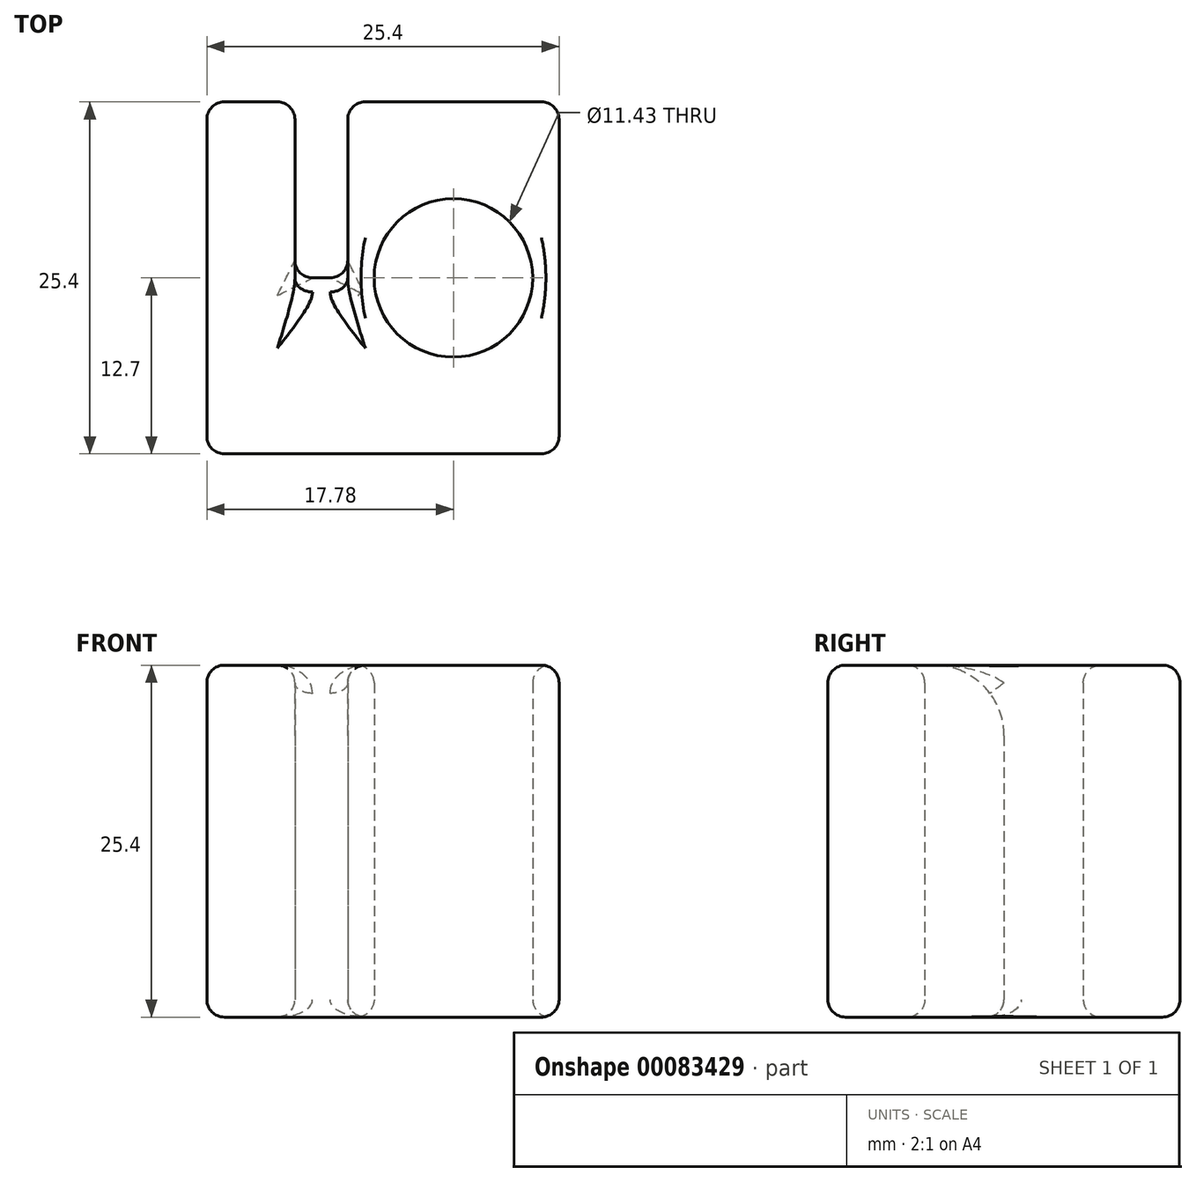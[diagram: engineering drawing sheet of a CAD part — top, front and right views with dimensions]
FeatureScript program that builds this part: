
annotation { "Feature Type Name" : "Feature", "Feature Type Description" : "" }
export const myFeature = defineFeature(function(context is Context, id is Id, definition is map)
    precondition{}
    {
        {
            var Q0;
            Q0=qCreatedBy(makeId("Top.planeOp"),FACE);
            var sketch = newSketch(context, id + "F0", { "sketchPlane" : qUnion([Q0])});
            skLineSegment(sketch, "E0.bottom", {"start": v(-12.7, -12.7) * mm, "end": v(12.7, -12.7) * mm});
            skLineSegment(sketch, "E0.top", {"start": v(-12.7, 12.7) * mm, "end": v(12.7, 12.7) * mm});
            skLineSegment(sketch, "E0.left", {"start": v(-12.7, -12.7) * mm, "end": v(-12.7, 12.7) * mm});
            skLineSegment(sketch, "E0.right", {"start": v(12.7, -12.7) * mm, "end": v(12.7, 12.7) * mm});
            skPoint(sketch, "E0.middle", {"position": v(0, 0) * mm});
            skLineSegment(sketch, "E1.bottom", {"start": v(-6.35, 12.7) * mm, "end": v(-2.54, 12.7) * mm});
            skLineSegment(sketch, "E1.top", {"start": v(-6.35, 0) * mm, "end": v(-2.54, 0) * mm});
            skLineSegment(sketch, "E1.left", {"start": v(-6.35, 12.7) * mm, "end": v(-6.35, 0) * mm});
            skLineSegment(sketch, "E1.right", {"start": v(-2.54, 12.7) * mm, "end": v(-2.54, 0) * mm});
            skCircle(sketch, "E2", {"center": v(5.08, 0) * mm, "radius": 5.72 * mm});
            skPoint(sketch, "E2.centerSnap0", {"position": v(12.7, 0) * mm});
            skLineSegment(sketch, "E3", {"start": v(12.7, 0) * mm, "end": v(-12.7, 0) * mm, "construction": true});
            skSolve(sketch);
        }
        {
            var Q0;
            Q0=makeQuery(id+"F0.imprint","IMPRINT",FACE,{"disambiguationData":[TD([[makeQuery(id+"F0.imprint","IMPRINT",EDGE,{"derivedFrom":sQuery(id+"F0.wireOp",EDGE,"E0.bottom")}),1.0]])]});
            extrude(context, id + "F1", {"entities" : qUnion([Q0]), "depth" : 25.4 * mm});
        }
        {
            var Q0;
            Q0=makeQuery(id+"F1.opExtrude","CAP_EDGE",EDGE,{"disambiguationData":[OSD([sQuery(id+"F0.wireOp",EDGE,"E1.top")])],"isStart":false});
            fillet(context, id + "F2", {"entities" : qUnion([Q0]), "radius" : 5.08 * mm, "tangentPropagation" : true, "allowEdgeOverflow" : false});
        }
        {
            var Q0;
            Q0=makeQuery(id+"F1.opExtrude","CAP_FACE",FACE,{"disambiguationData":[OSD([sQuery(id+"F0.wireOp",EDGE,"E0.bottom"),sQuery(id+"F0.wireOp",EDGE,"E0.top"),sQuery(id+"F0.wireOp",EDGE,"E0.left"),sQuery(id+"F0.wireOp",EDGE,"E0.right"),sQuery(id+"F0.wireOp",EDGE,"E1.top"),sQuery(id+"F0.wireOp",EDGE,"E1.left"),sQuery(id+"F0.wireOp",EDGE,"E1.right"),sQuery(id+"F0.wireOp",EDGE,"E2")])],"isStart":false});
            var Q1;
            {var subQ0=sQuery(id+"F0.wireOp",EDGE,"E0.top");Q1=makeQuery(id+"F1.opExtrude","SWEPT_FACE",FACE,{"disambiguationData":[OSD([subQ0]),TDD([makeQuery(id+"F0.imprint","IMPRINT",EDGE,{"disambiguationData":[TD([[makeQuery(id+"F0.imprint","INTERSECT",VERTEX,{"derivedFrom":[subQ0,sQuery(id+"F0.wireOp",EDGE,"E0.right")]}),1.0]])],"derivedFrom":subQ0})])]});}
            var Q2;
            {var subQ0=sQuery(id+"F0.wireOp",EDGE,"E0.top");Q2=makeQuery(id+"F1.opExtrude","SWEPT_FACE",FACE,{"disambiguationData":[OSD([subQ0]),TDD([makeQuery(id+"F0.imprint","IMPRINT",EDGE,{"disambiguationData":[TD([[makeQuery(id+"F0.imprint","INTERSECT",VERTEX,{"derivedFrom":[subQ0,sQuery(id+"F0.wireOp",EDGE,"E0.left")]}),-1.0]])],"derivedFrom":subQ0})])]});}
            var Q3;
            Q3=makeQuery(id+"F1.opExtrude","SWEPT_FACE",FACE,{"disambiguationData":[OSD([sQuery(id+"F0.wireOp",EDGE,"E0.bottom")])]});
            var Q4;
            Q4=makeQuery(id+"F1.opExtrude","CAP_FACE",FACE,{"disambiguationData":[OSD([sQuery(id+"F0.wireOp",EDGE,"E0.bottom"),sQuery(id+"F0.wireOp",EDGE,"E0.top"),sQuery(id+"F0.wireOp",EDGE,"E0.left"),sQuery(id+"F0.wireOp",EDGE,"E0.right"),sQuery(id+"F0.wireOp",EDGE,"E1.top"),sQuery(id+"F0.wireOp",EDGE,"E1.left"),sQuery(id+"F0.wireOp",EDGE,"E1.right"),sQuery(id+"F0.wireOp",EDGE,"E2")])],"isStart":true});
            fillet(context, id + "F3", {"entities" : qUnion([Q0, Q1, Q2, Q3, Q4]), "radius" : 1.27 * mm, "tangentPropagation" : true, "allowEdgeOverflow" : false});
        }
        {
            var Q0;
            Q0=makeQuery(id+"F1.opExtrude","SWEPT_EDGE",EDGE,{"disambiguationData":[OSD([sQuery(id+"F0.wireOp",EDGE,"E1.top"),sQuery(id+"F0.wireOp",EDGE,"E1.left")])]});
            var Q1;
            Q1=makeQuery(id+"F1.opExtrude","SWEPT_EDGE",EDGE,{"disambiguationData":[OSD([sQuery(id+"F0.wireOp",EDGE,"E1.top"),sQuery(id+"F0.wireOp",EDGE,"E1.right")])]});
            fillet(context, id + "F4", {"entities" : qUnion([Q0, Q1]), "radius" : 1.27 * mm, "tangentPropagation" : true, "allowEdgeOverflow" : false});
        }
    });
